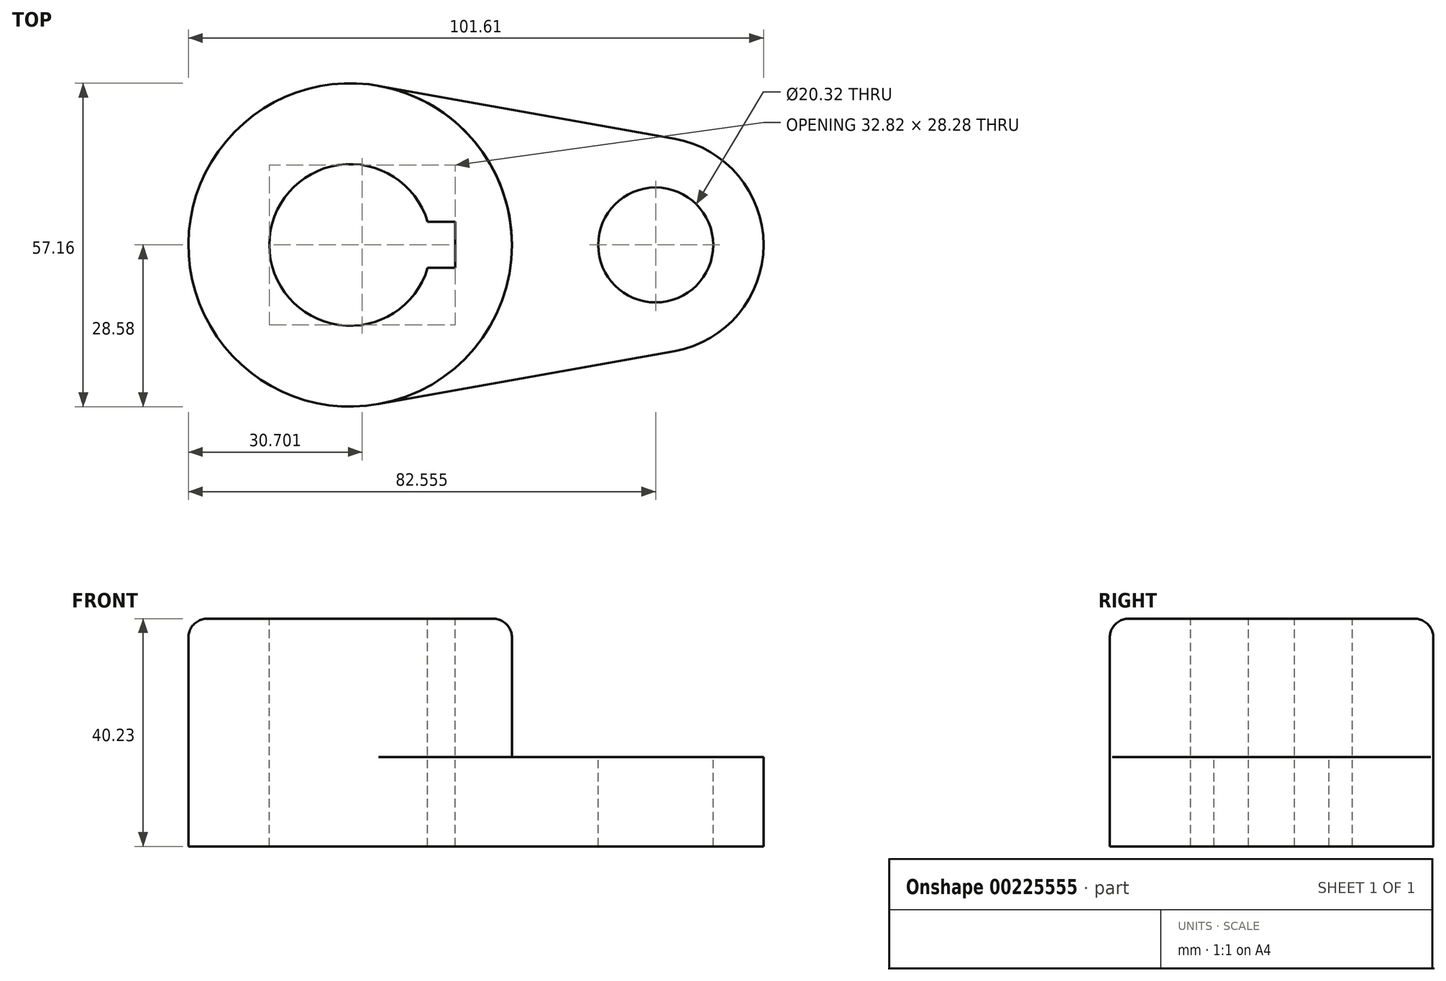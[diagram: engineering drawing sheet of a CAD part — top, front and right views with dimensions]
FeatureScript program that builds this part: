
annotation { "Feature Type Name" : "Feature", "Feature Type Description" : "" }
export const myFeature = defineFeature(function(context is Context, id is Id, definition is map)
    precondition{}
    {
        {
            var Q0;
            Q0=qCreatedBy(makeId("Top.planeOp"),FACE);
            var sketch = newSketch(context, id + "F0", { "sketchPlane" : qUnion([Q0])});
            skCircle(sketch, "E0", {"center": v(0, 0) * mm, "radius": 28.58 * mm});
            skSolve(sketch);
        }
        {
            var Q0;
            Q0 = qSketchRegion(id + "F0", true);
            extrude(context, id + "F1", {"entities" : qUnion([Q0]), "depth" : 40.23 * mm});
        }
        {
            var Q0;
            Q0=qCreatedBy(makeId("Top.planeOp"),FACE);
            var sketch = newSketch(context, id + "F2", { "sketchPlane" : qUnion([Q0])});
            skLineSegment(sketch, "E1", {"start": v(53.98, 0) * mm, "end": v(53.98, -36.04) * mm, "construction": true});
            skLineSegment(sketch, "E2", {"start": v(53.98, -36.04) * mm, "end": v(53.98, 27.42) * mm, "construction": true});
            skArc(sketch, "E3", {"start": v(53.98, -19.05) * mm, "mid": v(73.03, 0) * mm, "end": v(53.98, 19.05) * mm});
            skLineSegment(sketch, "E4", {"start": v(5.04, -28.13) * mm, "end": v(57.34, -18.75) * mm});
            skArc(sketch, "E5", {"start": v(5.04, 28.13) * mm, "mid": v(-28.58, 0) * mm, "end": v(5.04, -28.13) * mm});
            skLineSegment(sketch, "E6", {"start": v(-19.16, 0) * mm, "end": v(100.57, 0) * mm, "construction": true});
            skLineSegment(sketch, "E7.MirrorCS", {"start": v(5.04, 28.13) * mm, "end": v(57.34, 18.75) * mm});
            skSolve(sketch);
        }
        {
            var Q0;
            Q0 = qSketchRegion(id + "F2", true);
            extrude(context, id + "F3", {"entities" : qUnion([Q0]), "operationType" : NewBodyOperationType.ADD, "depth" : 15.77 * mm});
        }
        {
            var Q0;
            Q0=makeQuery(id+"F1.opExtrude","CAP_FACE",FACE,{"disambiguationData":[OSD([sQuery(id+"F0.wireOp",EDGE,"E0")])],"isStart":false});
            var sketch = newSketch(context, id + "F4", { "sketchPlane" : qUnion([Q0])});
            skLineSegment(sketch, "E8", {"start": v(-14.29, 0) * mm, "end": v(18.53, 0) * mm, "construction": true});
            skLineSegment(sketch, "E9", {"start": v(13.7, 4.06) * mm, "end": v(18.53, 4.06) * mm});
            skLineSegment(sketch, "E10", {"start": v(18.53, 4.06) * mm, "end": v(18.53, 0) * mm});
            skLineSegment(sketch, "E11.MirrorCS", {"start": v(13.7, -4.06) * mm, "end": v(18.53, -4.06) * mm});
            skLineSegment(sketch, "E12.MirrorCS", {"start": v(18.53, -4.06) * mm, "end": v(18.53, 0) * mm});
            skPoint(sketch, "E13.orphan", {"position": v(0, 4.06) * mm});
            skPoint(sketch, "E14.orphan", {"position": v(0, -4.06) * mm});
            skArc(sketch, "E15", {"start": v(13.7, 4.06) * mm, "mid": v(-14.29, 0) * mm, "end": v(13.7, -4.06) * mm});
            skSolve(sketch);
        }
        {
            var Q0;
            Q0 = qSketchRegion(id + "F4", true);
            extrude(context, id + "F5", {"entities" : qUnion([Q0]), "operationType" : NewBodyOperationType.REMOVE, "endBound" : BoundingType.THROUGH_ALL, "oppositeDirection" : true, "depth" : 25.4 * mm});
        }
        {
            var Q0;
            Q0=makeQuery(id+"F3.opExtrude","CAP_FACE",FACE,{"disambiguationData":[OSD([sQuery(id+"F2.wireOp",EDGE,"E3"),sQuery(id+"F2.wireOp",EDGE,"E4"),sQuery(id+"F2.wireOp",EDGE,"E5"),sQuery(id+"F2.wireOp",EDGE,"E7.MirrorCS")])],"isStart":false});
            var sketch = newSketch(context, id + "F6", { "sketchPlane" : qUnion([Q0])});
            skCircle(sketch, "E16", {"center": v(53.98, 0) * mm, "radius": 10.16 * mm});
            skSolve(sketch);
        }
        {
            var Q0;
            Q0 = qSketchRegion(id + "F6", true);
            extrude(context, id + "F7", {"entities" : qUnion([Q0]), "operationType" : NewBodyOperationType.REMOVE, "endBound" : BoundingType.THROUGH_ALL, "oppositeDirection" : true, "depth" : 25.4 * mm});
        }
        {
            var Q0;
            Q0=makeQuery(id+"F1.opExtrude","CAP_EDGE",EDGE,{"disambiguationData":[OSD([sQuery(id+"F0.wireOp",EDGE,"E0")])],"isStart":false});
            fillet(context, id + "F8", {"entities" : qUnion([Q0]), "radius" : 3.3 * mm, "tangentPropagation" : true, "allowEdgeOverflow" : false});
        }
    });
